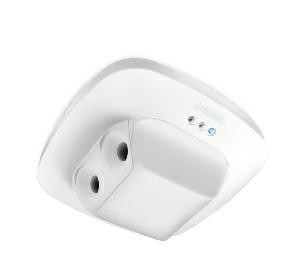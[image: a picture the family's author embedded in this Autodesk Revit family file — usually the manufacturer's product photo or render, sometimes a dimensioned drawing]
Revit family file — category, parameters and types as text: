
# Revit family: single_us_057503
name_source: partatom
category: Elektroinstallationen
revit_build: Autodesk Revit 2016 (Build: 20190508_0715(x64)
units: mm (PartAtom-declared; Revit-internal decimal feet)

## family parameters
Basisbauteil = Fläche
Beim Laden mit Abzugskörper schneiden = Nein
Bemaßung runder Anschluss = Durchmesser verwenden
Beschriftungsausrichtung beibehalten = Nein
Gemeinsam genutzt = Nein
Raumberechnungspunkt = Nein
Teiletyp = Normal

## types (1)
- Single US
    Apparent Load = 0 VA
    Beschreibung = Type: Presence detector; Dimensions (L x W x H): 73 x 120 x 120 mm; Mains power supply: 16 V; Sensor Technology: Ultrasonic; Application, place: Indoors; Application, room: corridor / aisle, stairwell, Indoors; Installation site: ceiling; Installation: Concealed wiring; Electronic scalability: Yes; Mechanical scalability: No; Mounting height: 2,50 – 3,50 m; Optimum mounting height: 2,5 m; Detection angle: 180 °; Sneak-by guard: Yes; Reach, radial: 10 x 3 m (30 m²); Reach, tangential: 10 x 3 m (30 m²); Twilight setting TEACH: Yes; Twilight setting: 10 – 1000 lx; Control output, Dali: Addressable/slave; Basic light level function: No; With bus coupling: Yes; Settings via: Bus; Interconnection: Yes; Material: Plastic; Ambient temperature: -25 – +55 °C; Colour: white; Colour, RAL: 9010; Manufacturer's Warranty: 5 years; Version: DALI-2 Input Device; PU1, EAN: 4007841057503
    Height = 0 mm  [stored 0 ft]
    Hersteller = Steinel
    Length = 73 mm
    Maximum range = 10.662 m
    ModVariant = Nein
    Modell = 057503
    Mounting Place = Ceiling
    Mounting Type = Recessed
    Number of Poles = 1
    OnlyDefault = Ja
    Power Factor = 1
    Product Name = Single US
    Product group = Presence detector
    ProductGroupID = 4
    Protection Class = Protection class
    Protection Degree = Degree of protection
    RlxData = <blob elided: 120141 chars, md5=f53d23ea>
    Sensor characteristics = Stretched
    Sensor type = Passive (infrared)
    SensorDataFile = <blob elided: 159730 chars, md5=e60cc4e0>
    Type of entry = Motion
    Typenbild = produkt1_057503.jpg
    Typenkommentare = Product without accessories
    URL = http://relux.com
    VarID = ---
    Voltage = 0 V
    Vorgabe-Ansicht = 1800 mm
    Weight = 0.00 kg
    Width = 120 mm  [stored 0.393701 ft]

note: [stored X ft] marks values corroborated as IEEE doubles in the binary element streams (Revit-internal decimal feet)

## geometry (parser evidence)
native form markers: Blend x4, Sweep x17
no freeform markers — native parametric forms only
